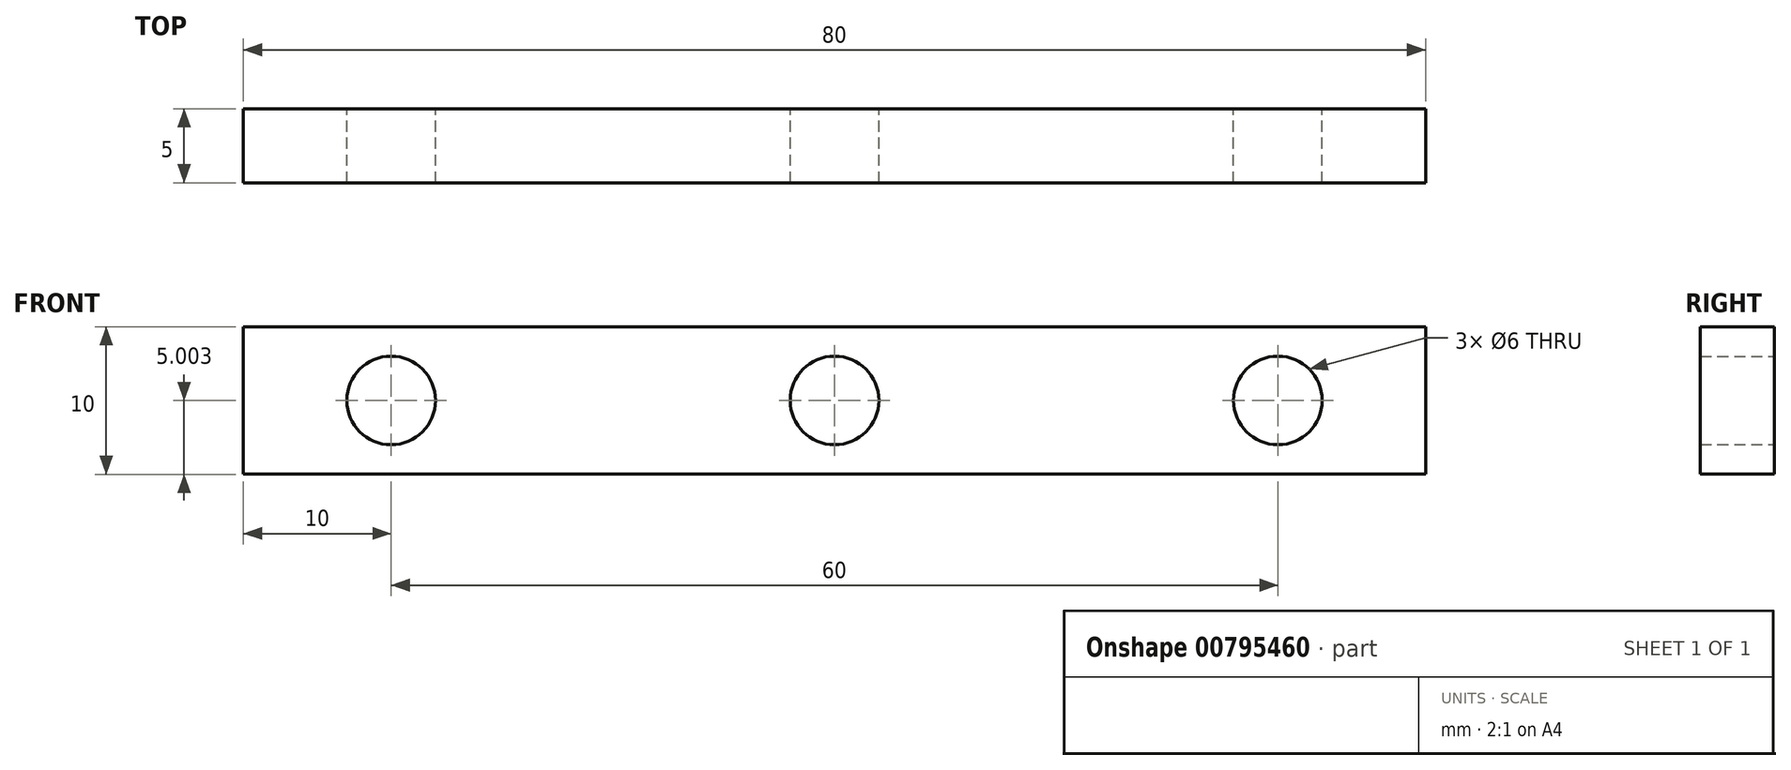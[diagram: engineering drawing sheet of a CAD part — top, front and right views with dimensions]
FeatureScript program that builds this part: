
annotation { "Feature Type Name" : "Feature", "Feature Type Description" : "" }
export const myFeature = defineFeature(function(context is Context, id is Id, definition is map)
    precondition{}
    {
        {
            var Q0;
            Q0=qCreatedBy(makeId("Front.planeOp"),FACE);
            var sketch = newSketch(context, id + "F0", { "sketchPlane" : qUnion([Q0])});
            skLineSegment(sketch, "E0.bottom", {"start": v(-40, -1.1) * mm, "end": v(40, -1.1) * mm});
            skLineSegment(sketch, "E0.top", {"start": v(-40, -11.1) * mm, "end": v(40, -11.1) * mm});
            skLineSegment(sketch, "E0.left", {"start": v(-40, -1.1) * mm, "end": v(-40, -11.1) * mm});
            skLineSegment(sketch, "E1", {"start": v(40, -1.1) * mm, "end": v(40, -11.1) * mm});
            skPoint(sketch, "E2", {"position": v(-55, -11.1) * mm});
            skPoint(sketch, "E3", {"position": v(-30, -6.1) * mm});
            skPoint(sketch, "E3.positionSnap0", {"position": v(-40, -6.1) * mm});
            skPoint(sketch, "E4", {"position": v(30, -6.1) * mm});
            skPoint(sketch, "E4.positionSnap0", {"position": v(40, -6.1) * mm});
            skPoint(sketch, "E5", {"position": v(0, -6.1) * mm});
            skCircle(sketch, "E6", {"center": v(-30, -6.1) * mm, "radius": 3 * mm});
            skCircle(sketch, "E7", {"center": v(0, -6.1) * mm, "radius": 3 * mm});
            skCircle(sketch, "E8", {"center": v(30, -6.1) * mm, "radius": 3 * mm});
            skSolve(sketch);
        }
        {
            var Q0;
            Q0=qSketchRegion(id+"F0",true);
            extrude(context, id + "F1", {"entities" : qUnion([Q0]), "depth" : 5 * mm, "offsetDistance" : 25 * mm});
        }
    });
